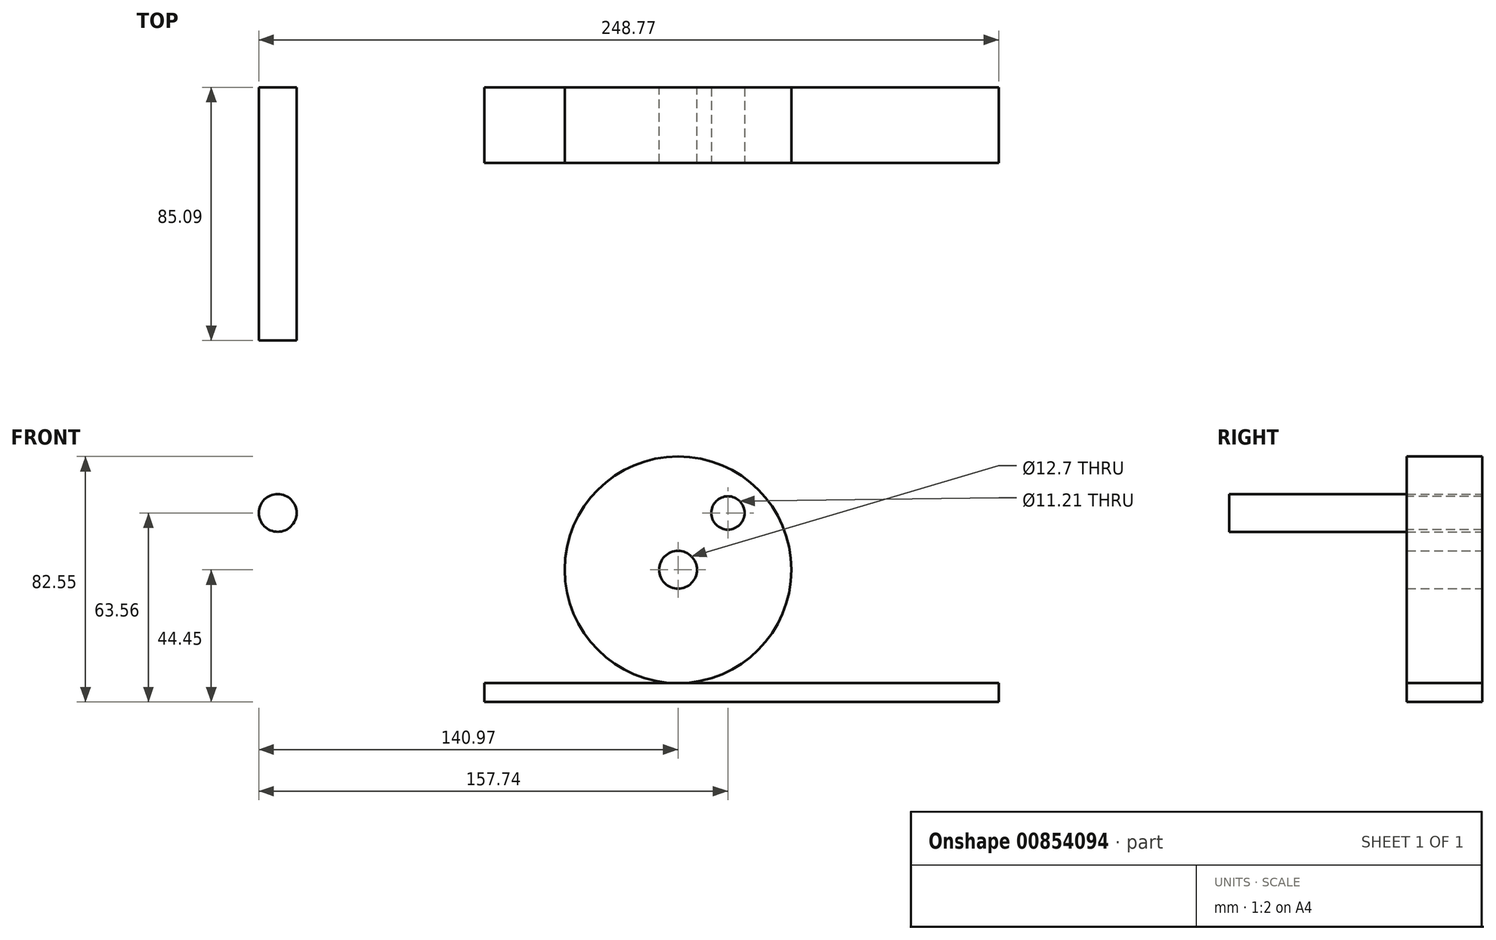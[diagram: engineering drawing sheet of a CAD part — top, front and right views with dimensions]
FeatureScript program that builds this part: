
annotation { "Feature Type Name" : "Feature", "Feature Type Description" : "" }
export const myFeature = defineFeature(function(context is Context, id is Id, definition is map)
    precondition{}
    {
        {
            var Q0;
            Q0=qCreatedBy(makeId("Front.planeOp"),FACE);
            var sketch = newSketch(context, id + "F0", { "sketchPlane" : qUnion([Q0])});
            skCircle(sketch, "E0", {"center": v(0, 0) * mm, "radius": 38.1 * mm});
            skCircle(sketch, "E1", {"center": v(0, 0) * mm, "radius": 6.35 * mm});
            skSolve(sketch);
        }
        {
            var Q0;
            Q0=makeQuery(id+"F0.imprint","IMPRINT",FACE,{"disambiguationData":[TD([[makeQuery(id+"F0.imprint","IMPRINT",EDGE,{"derivedFrom":sQuery(id+"F0.wireOp",EDGE,"E0")}),1.0]])]});
            extrude(context, id + "F1", {"entities" : qUnion([Q0]), "depth" : 25.4 * mm, "offsetDistance" : 25.4 * mm});
        }
        {
            var Q0;
            Q0=qCreatedBy(makeId("Front.planeOp"),FACE);
            var sketch = newSketch(context, id + "F2", { "sketchPlane" : qUnion([Q0])});
            skLineSegment(sketch, "E2", {"start": v(-65.11, -38.1) * mm, "end": v(107.8, -38.1) * mm});
            skLineSegment(sketch, "E3.0", {"start": v(-65.11, -44.45) * mm, "end": v(107.8, -44.45) * mm});
            skLineSegment(sketch, "E4", {"start": v(-65.11, -38.1) * mm, "end": v(-65.11, -44.45) * mm});
            skLineSegment(sketch, "E5", {"start": v(107.8, -38.1) * mm, "end": v(107.8, -44.45) * mm});
            skSolve(sketch);
        }
        {
            var Q0;
            Q0=makeQuery(id+"F2.imprint","IMPRINT",FACE,{"disambiguationData":[TD([[makeQuery(id+"F2.imprint","IMPRINT",EDGE,{"derivedFrom":sQuery(id+"F2.wireOp",EDGE,"E2")}),-1.0]])]});
            extrude(context, id + "F3", {"entities" : qUnion([Q0]), "depth" : 25.4 * mm, "offsetDistance" : 25.4 * mm});
        }
        {
            var Q0;
            Q0=qCreatedBy(makeId("Front.planeOp"),FACE);
            var sketch = newSketch(context, id + "F4", { "sketchPlane" : qUnion([Q0])});
            skCircle(sketch, "E6", {"center": v(-134.62, 19.11) * mm, "radius": 6.35 * mm});
            skSolve(sketch);
        }
        {
            var Q0;
            Q0=makeQuery(id+"F4.imprint","IMPRINT",FACE,{"disambiguationData":[TD([[makeQuery(id+"F4.imprint","IMPRINT",EDGE,{"derivedFrom":sQuery(id+"F4.wireOp",EDGE,"E6")}),1.0]])]});
            extrude(context, id + "F5", {"entities" : qUnion([Q0]), "depth" : 85.1 * mm, "offsetDistance" : 25.4 * mm});
        }
        {
            var Q0;
            Q0=makeQuery(id+"F1.opExtrude","CAP_FACE",FACE,{"disambiguationData":[OSD([sQuery(id+"F0.wireOp",EDGE,"E0"),sQuery(id+"F0.wireOp",EDGE,"E1")])],"isStart":false});
            var sketch = newSketch(context, id + "F6", { "sketchPlane" : qUnion([Q0])});
            skCircle(sketch, "E7", {"center": v(16.77, 19.1) * mm, "radius": 5.6 * mm});
            skSolve(sketch);
        }
        {
            var Q0;
            Q0=makeQuery(id+"F6.imprint","IMPRINT",FACE,{"disambiguationData":[TD([[makeQuery(id+"F6.imprint","IMPRINT",EDGE,{"derivedFrom":sQuery(id+"F6.wireOp",EDGE,"E7")}),1.0]])]});
            extrude(context, id + "F7", {"entities" : qUnion([Q0]), "operationType" : NewBodyOperationType.REMOVE, "oppositeDirection" : true, "depth" : 25.4 * mm, "offsetDistance" : 25.4 * mm});
        }
    });
